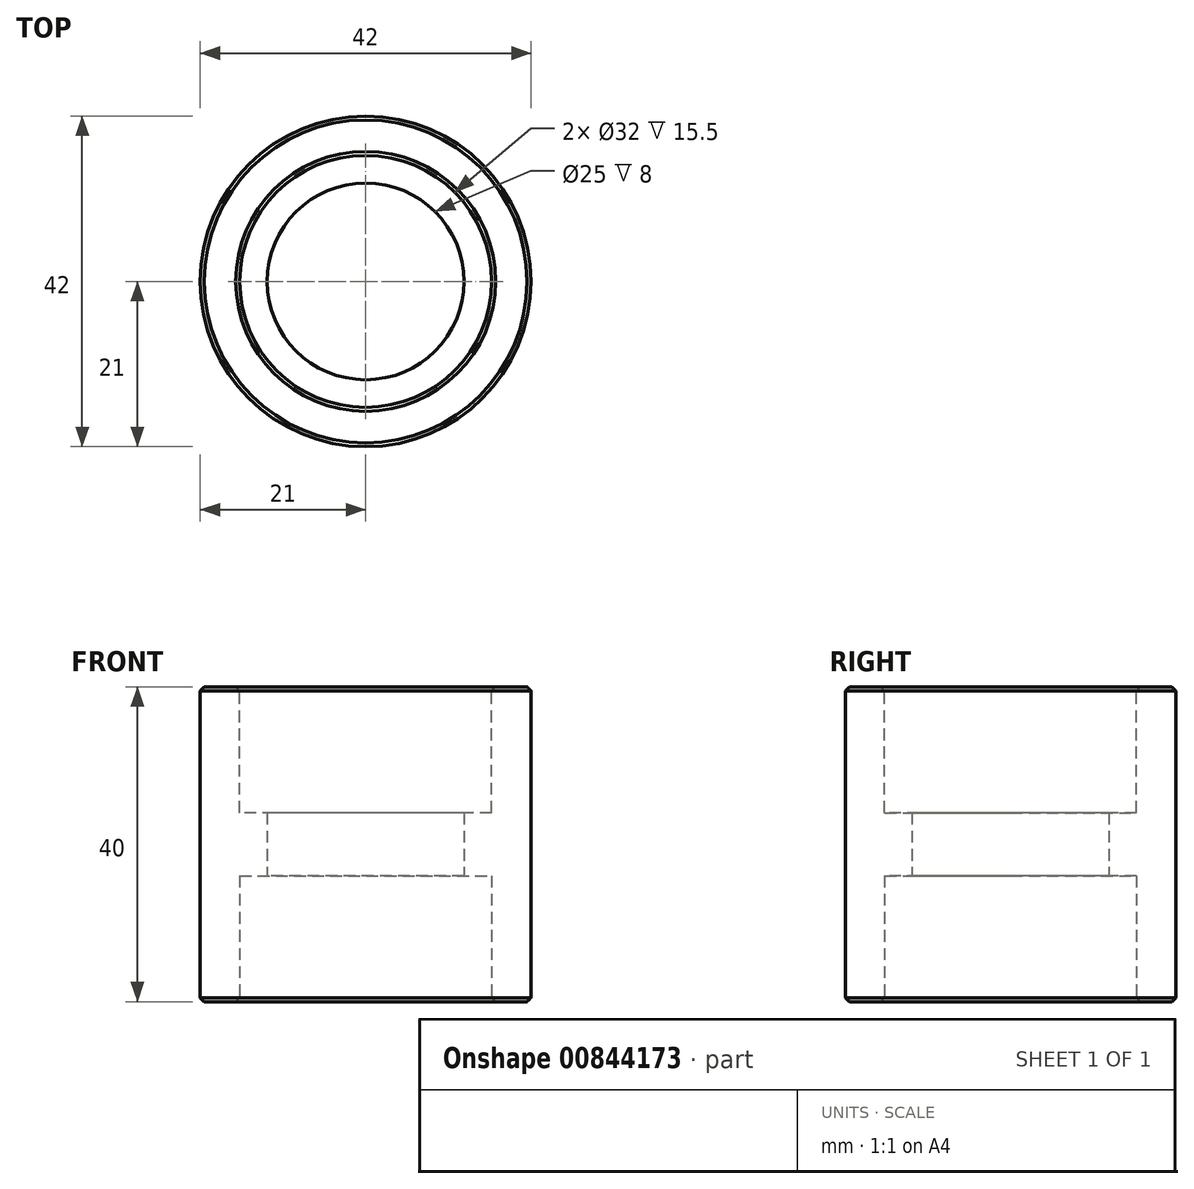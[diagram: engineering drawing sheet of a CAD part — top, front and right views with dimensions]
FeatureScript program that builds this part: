
annotation { "Feature Type Name" : "Feature", "Feature Type Description" : "" }
export const myFeature = defineFeature(function(context is Context, id is Id, definition is map)
    precondition{}
    {
        {
            var Q0;
            Q0=qCreatedBy(makeId("Top.planeOp"),FACE);
            var sketch = newSketch(context, id + "F0", { "sketchPlane" : qUnion([Q0])});
            skCircle(sketch, "E0", {"center": v(0, 0) * mm, "radius": 21 * mm});
            skCircle(sketch, "E1", {"center": v(0, 0) * mm, "radius": 12.5 * mm});
            skSolve(sketch);
        }
        {
            var Q0;
            Q0=makeQuery(id+"F0.imprint","IMPRINT",FACE,{"disambiguationData":[TD([[makeQuery(id+"F0.imprint","IMPRINT",EDGE,{"derivedFrom":sQuery(id+"F0.wireOp",EDGE,"E0")}),1.0]])]});
            extrude(context, id + "F1", {"entities" : qUnion([Q0]), "depth" : 40 * mm, "offsetDistance" : 25 * mm});
        }
        {
            var Q0;
            Q0=makeQuery(id+"F1.opExtrude","CAP_FACE",FACE,{"disambiguationData":[OSD([sQuery(id+"F0.wireOp",EDGE,"E0"),sQuery(id+"F0.wireOp",EDGE,"E1")])],"isStart":false});
            var sketch = newSketch(context, id + "F2", { "sketchPlane" : qUnion([Q0])});
            skCircle(sketch, "E2", {"center": v(0, 0) * mm, "radius": 16 * mm});
            skSolve(sketch);
        }
        {
            var Q0;
            Q0 = qSketchRegion(id + "F2", true);
            extrude(context, id + "F3", {"entities" : qUnion([Q0]), "operationType" : NewBodyOperationType.REMOVE, "oppositeDirection" : true, "depth" : 16 * mm, "offsetDistance" : 25 * mm});
        }
        {
            var Q0;
            Q0=makeQuery(id+"F1.opExtrude","CAP_FACE",FACE,{"disambiguationData":[OSD([sQuery(id+"F0.wireOp",EDGE,"E0"),sQuery(id+"F0.wireOp",EDGE,"E1")])],"isStart":true});
            var sketch = newSketch(context, id + "F4", { "sketchPlane" : qUnion([Q0])});
            skCircle(sketch, "E3", {"center": v(0, 0) * mm, "radius": 16 * mm});
            skSolve(sketch);
        }
        {
            var Q0;
            Q0=makeQuery(id+"F4.imprint","IMPRINT",FACE,{"disambiguationData":[TD([[makeQuery(id+"F4.imprint","IMPRINT",EDGE,{"derivedFrom":sQuery(id+"F4.wireOp",EDGE,"E3")}),1.0]])]});
            extrude(context, id + "F5", {"entities" : qUnion([Q0]), "operationType" : NewBodyOperationType.REMOVE, "oppositeDirection" : true, "depth" : 16 * mm, "offsetDistance" : 25 * mm});
        }
        {
            var Q0;
            Q0=makeQuery(id+"F1.opExtrude","CAP_FACE",FACE,{"disambiguationData":[OSD([sQuery(id+"F0.wireOp",EDGE,"E0"),sQuery(id+"F0.wireOp",EDGE,"E1")])],"isStart":true});
            var Q1;
            Q1=makeQuery(id+"F1.opExtrude","CAP_FACE",FACE,{"disambiguationData":[OSD([sQuery(id+"F0.wireOp",EDGE,"E0"),sQuery(id+"F0.wireOp",EDGE,"E1")])],"isStart":false});
            chamfer(context, id + "F6", {"entities" : qUnion([Q0, Q1]), "width" : .5 * mm, "tangentPropagation" : true});
        }
    });
